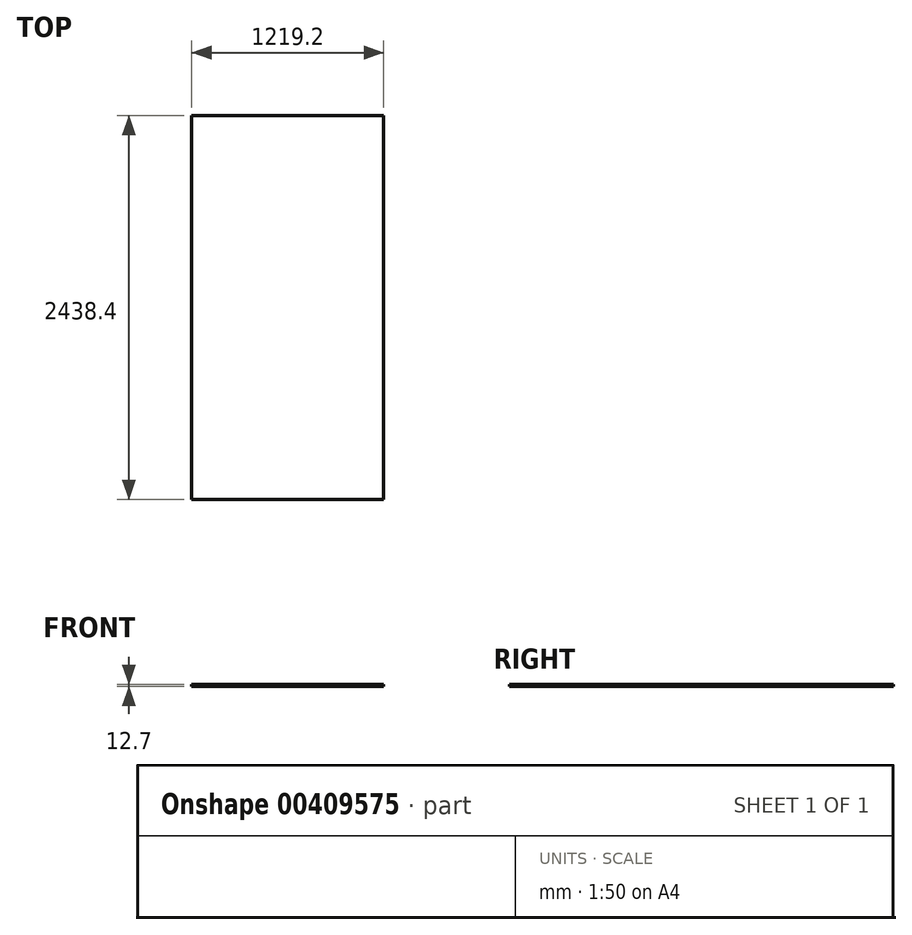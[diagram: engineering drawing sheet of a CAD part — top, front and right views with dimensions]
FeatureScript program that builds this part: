
annotation { "Feature Type Name" : "Feature", "Feature Type Description" : "" }
export const myFeature = defineFeature(function(context is Context, id is Id, definition is map)
    precondition{}
    {
        {
            var Q0;
            Q0=qCreatedBy(makeId("Top.planeOp"),FACE);
            var sketch = newSketch(context, id + "F0", { "sketchPlane" : qUnion([Q0])});
            skLineSegment(sketch, "E0.bottom", {"start": v(-634.47, 1976.16) * mm, "end": v(584.73, 1976.16) * mm});
            skLineSegment(sketch, "E0.top", {"start": v(-634.47, -462.24) * mm, "end": v(584.73, -462.24) * mm});
            skLineSegment(sketch, "E0.left", {"start": v(-634.47, 1976.16) * mm, "end": v(-634.47, -462.24) * mm});
            skLineSegment(sketch, "E0.right", {"start": v(584.73, 1976.16) * mm, "end": v(584.73, -462.24) * mm});
            skSolve(sketch);
        }
        {
            var Q0;
            Q0=makeQuery(id+"F0.imprint","IMPRINT",FACE,{"disambiguationData":[TD([[makeQuery(id+"F0.imprint","IMPRINT",EDGE,{"derivedFrom":sQuery(id+"F0.wireOp",EDGE,"E0.bottom")}),-1.0]])]});
            extrude(context, id + "F1", {"entities" : qUnion([Q0]), "depth" : 12.7 * mm});
        }
    });
